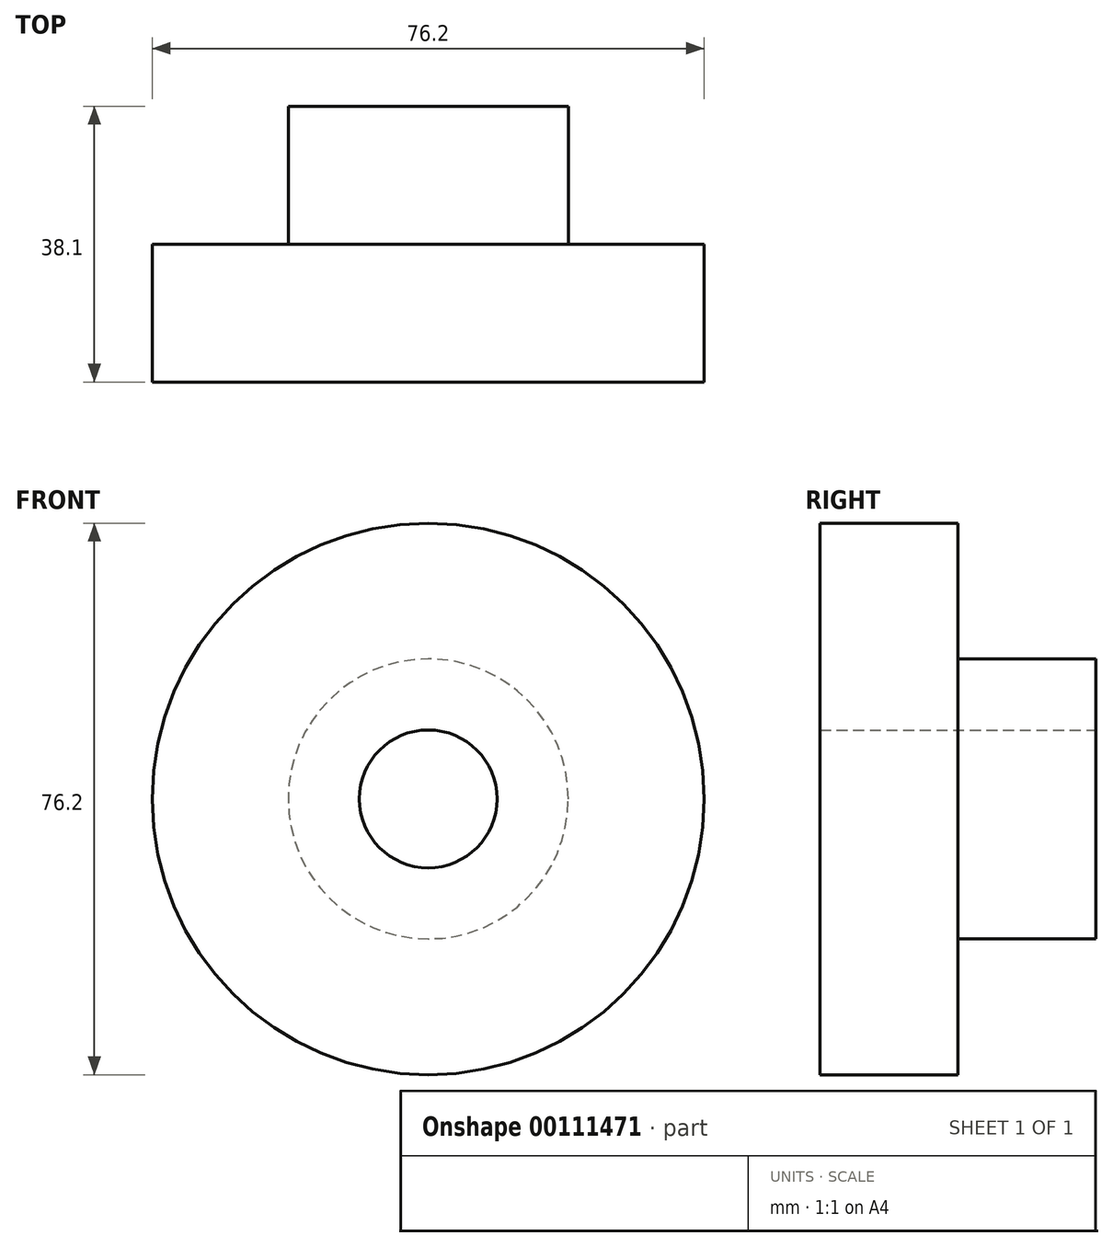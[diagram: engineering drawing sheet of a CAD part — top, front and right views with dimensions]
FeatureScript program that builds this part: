
annotation { "Feature Type Name" : "Feature", "Feature Type Description" : "" }
export const myFeature = defineFeature(function(context is Context, id is Id, definition is map)
    precondition{}
    {
        {
            var Q0;
            Q0=qCreatedBy(makeId("Front.planeOp"),FACE);
            var sketch = newSketch(context, id + "F0", { "sketchPlane" : qUnion([Q0])});
            skCircle(sketch, "E0", {"center": v(0, 0) * mm, "radius": 38.1 * mm});
            skSolve(sketch);
        }
        {
            var Q0;
            Q0 = qSketchRegion(id + "F0", true);
            extrude(context, id + "F1", {"entities" : qUnion([Q0]), "depth" : 19.05 * mm});
        }
        {
            var Q0;
            Q0=makeQuery(id+"F1.opExtrude","CAP_FACE",FACE,{"disambiguationData":[OSD([sQuery(id+"F0.wireOp",EDGE,"E0")])],"isStart":true});
            var sketch = newSketch(context, id + "F2", { "sketchPlane" : qUnion([Q0])});
            skCircle(sketch, "E1", {"center": v(0, 0) * mm, "radius": 19.34 * mm});
            skSolve(sketch);
        }
        {
            var Q0;
            Q0 = qSketchRegion(id + "F2", true);
            extrude(context, id + "F3", {"entities" : qUnion([Q0]), "operationType" : NewBodyOperationType.ADD, "depth" : 19.05 * mm});
        }
        {
            var Q0;
            Q0=makeQuery(id+"F3.opExtrude","CAP_FACE",FACE,{"disambiguationData":[OSD([sQuery(id+"F2.wireOp",EDGE,"E1")])],"isStart":false});
            var sketch = newSketch(context, id + "F4", { "sketchPlane" : qUnion([Q0])});
            skCircle(sketch, "E2", {"center": v(0, 0) * mm, "radius": 9.52 * mm});
            skSolve(sketch);
        }
        {
            var Q0;
            Q0 = qSketchRegion(id + "F4", true);
            extrude(context, id + "F5", {"entities" : qUnion([Q0]), "operationType" : NewBodyOperationType.REMOVE, "endBound" : BoundingType.THROUGH_ALL, "oppositeDirection" : true, "depth" : 25.4 * mm});
        }
    });
